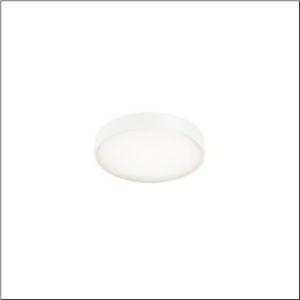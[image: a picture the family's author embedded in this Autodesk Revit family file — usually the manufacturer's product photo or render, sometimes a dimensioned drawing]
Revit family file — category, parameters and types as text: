
# Revit family: round_21_s_51mr34fd0421w
name_source: partatom
category: Lighting Fixtures
units: mm (PartAtom-declared; Revit-internal decimal feet)

## family parameters
Cut with Voids When Loaded = No
Host = Face
Light Source = No
Part Type = Normal
Room Calculation Point = No
Round Connector Dimension = Use Diameter
Shared = No

## types (1)
- Round 21 S (1 x LED, 3910 lm, 30.3 W, 4000K)
    Apparent Load = 30 VA
    CIE Flux Codes = 49 80 96 100 100
    Color Rendering = 80
    Color Temperature = 4000K
    Default Elevation = 1800 mm
    Description = Round 21 S, wall and ceiling luminaire, primary optical cover: cover, of PMMA, opal, light emission: direct distribution, primary light characteristic: symmetric, installation type: suspended mounting, surface-mounted, LED, rated luminous flux: 3.900lm, luminous efficacy: 129lm/W, light colour: 840, colour temperature: 4000K, control gear: DALI 2, with terminal, 5-pole, mains connection: 230V, AC, 50/60Hz, rated input power: 30.3W, housing, of aluminium, coated, white, diameter: 400mm, height: 62mm, protection rating (complete): IP40, insulation class (complete): insulation class I (protective earthing), certification: CE, impact resistance: IK04, permissible operating ambient temperature: -10..+35°C, packaging unit: 1 piece
    Height = 87 mm
    Lamp = 1 x LED
    Lamp Light Flux = 3910 lm
    Lamp Power = 30.3 W
    Lamp count = 1
    Length = 400 mm
    Luminous efficacy = 129 lm/W
    Manufacturer = Siteco
    ModVariant = No
    Model = 51MR34FD0421W
    Mounting Place = Ceiling
    Mounting Type = Surface mounted
    Number of Poles = 1
    OnlyDefault = Yes
    Power Factor = 1
    Product Name = Round 21 S
    Product group = wall and ceiling luminaire | ceiling mounted
    ProductGroupID = 304
    Protection Class = Protection class I
    Protection Degree = IP 40
    RLX_Detail_Level = 1
    RLX_Emergency_Light_Flux = 0 lm
    RLX_Emergency_Type = 0
    RLX_Emergency_Type_DB = No
    RlxData = <blob elided: 9529 chars, md5=d6401aa0>
    Socket = socket
    Standby Power = 0 W
    System Light Flux = 3910 lm
    System Power = 30 W
    Type Comments = Product without accessories
    Type Image = l_1258307.jpg
    URL = http://relux.com
    VarID = ---
    Voltage = 0 V
    Weight = 0.00 kg
    Width = 0 mm  [stored 0 ft]

note: [stored X ft] marks values corroborated as IEEE doubles in the binary element streams (Revit-internal decimal feet)

## geometry (parser evidence)
native form markers: Sweep x9
no freeform markers — native parametric forms only
